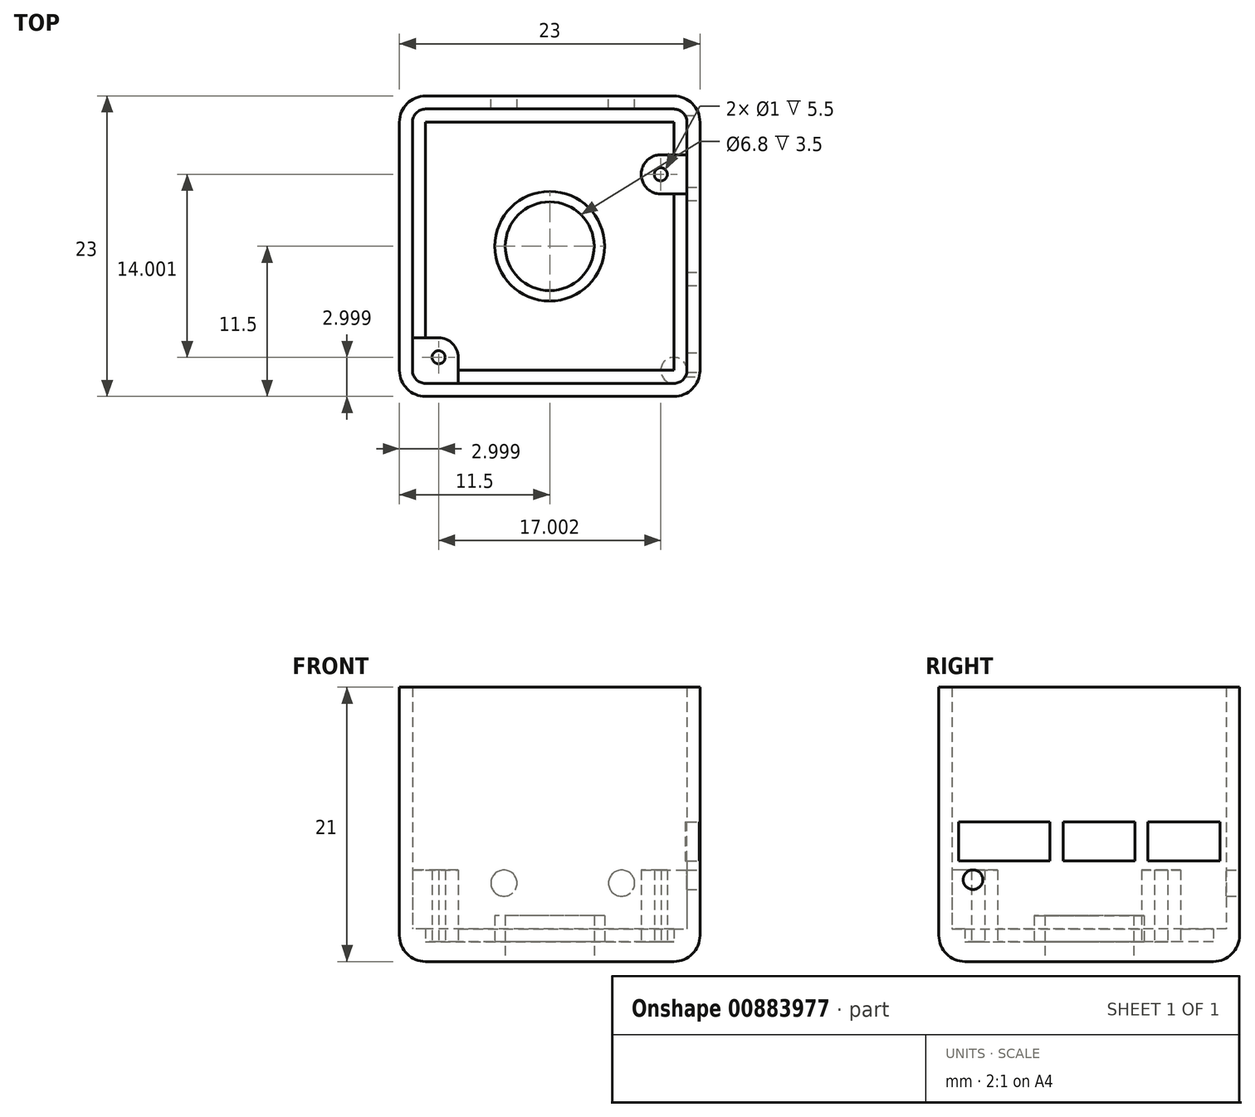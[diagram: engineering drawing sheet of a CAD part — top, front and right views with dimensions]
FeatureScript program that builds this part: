
annotation { "Feature Type Name" : "Feature", "Feature Type Description" : "" }
export const myFeature = defineFeature(function(context is Context, id is Id, definition is map)
    precondition{}
    {
        {
            var Q0;
            Q0=qCreatedBy(makeId("Top.planeOp"),FACE);
            var sketch = newSketch(context, id + "F0", { "sketchPlane" : qUnion([Q0])});
            skLineSegment(sketch, "E0.bottom", {"start": v(9.5, -11.5) * mm, "end": v(-9.5, -11.5) * mm});
            skLineSegment(sketch, "E0.top", {"start": v(9.5, 11.5) * mm, "end": v(-9.5, 11.5) * mm});
            skLineSegment(sketch, "E0.left", {"start": v(11.5, -9.5) * mm, "end": v(11.5, 9.5) * mm});
            skLineSegment(sketch, "E0.right", {"start": v(-11.5, -9.5) * mm, "end": v(-11.5, 9.5) * mm});
            skPoint(sketch, "E0.middle", {"position": v(0, 0) * mm});
            skCircle(sketch, "E1", {"center": v(0, 0) * mm, "radius": 3.4 * mm});
            skLineSegment(sketch, "E2.bottom", {"start": v(8.5, -8.5) * mm, "end": v(-8.5, -8.5) * mm});
            skLineSegment(sketch, "E2.top", {"start": v(8.5, 8.5) * mm, "end": v(-8.5, 8.5) * mm});
            skLineSegment(sketch, "E2.left", {"start": v(8.5, -8.5) * mm, "end": v(8.5, 8.5) * mm});
            skLineSegment(sketch, "E2.right", {"start": v(-8.5, -8.5) * mm, "end": v(-8.5, 8.5) * mm});
            skLineSegment(sketch, "E3", {"start": v(8.5, -8.5) * mm, "end": v(8.5, 5.5) * mm});
            skPoint(sketch, "E4.visualSharp", {"position": v(-11.5, -11.5) * mm});
            skArc(sketch, "E4.filletArc", {"start": v(-11.5, -9.5) * mm, "mid": v(-10.91, -10.91) * mm, "end": v(-9.5, -11.5) * mm});
            skPoint(sketch, "E5.visualSharp", {"position": v(11.5, -11.5) * mm});
            skArc(sketch, "E5.filletArc", {"start": v(9.5, -11.5) * mm, "mid": v(10.91, -10.91) * mm, "end": v(11.5, -9.5) * mm});
            skPoint(sketch, "E6.visualSharp", {"position": v(-11.5, 11.5) * mm});
            skArc(sketch, "E6.filletArc", {"start": v(-9.5, 11.5) * mm, "mid": v(-10.91, 10.91) * mm, "end": v(-11.5, 9.5) * mm});
            skPoint(sketch, "E7.visualSharp", {"position": v(11.5, 11.5) * mm});
            skArc(sketch, "E7.filletArc", {"start": v(11.5, 9.5) * mm, "mid": v(10.91, 10.91) * mm, "end": v(9.5, 11.5) * mm});
            skSolve(sketch);
        }
        {
            var Q0;
            Q0 = qSketchRegion(id + "F0", true);
            var Q1;
            Q1=makeQuery(id+"F0.imprint","IMPRINT",FACE,{"disambiguationData":[TD([[makeQuery(id+"F0.imprint","IMPRINT",EDGE,{"derivedFrom":sQuery(id+"F0.wireOp",EDGE,"E1")}),-1.0]])]});
            extrude(context, id + "F1", {"entities" : qUnion([Q0, Q1]), "depth" : 1.5 * mm, "offsetDistance" : 25 * mm});
        }
        {
            var Q0;
            Q0=makeQuery(id+"F1.opExtrude","CAP_FACE",FACE,{"disambiguationData":[OSD([sQuery(id+"F0.wireOp",EDGE,"E0.bottom"),sQuery(id+"F0.wireOp",EDGE,"E0.top"),sQuery(id+"F0.wireOp",EDGE,"E0.left"),sQuery(id+"F0.wireOp",EDGE,"E0.right"),sQuery(id+"F0.wireOp",EDGE,"E1")])],"isStart":false});
            var sketch = newSketch(context, id + "F2", { "sketchPlane" : qUnion([Q0])});
            skCircle(sketch, "E8", {"center": v(0, 0) * mm, "radius": 4.2 * mm});
            skCircle(sketch, "E9", {"center": v(-8.5, -8.5) * mm, "radius": 0.5 * mm});
            skArc(sketch, "E10", {"start": v(-7, -8.5) * mm, "mid": v(-7.44, -7.44) * mm, "end": v(-8.52, -7) * mm});
            skCircle(sketch, "E11", {"center": v(8.5, 5.5) * mm, "radius": 0.5 * mm});
            skArc(sketch, "E12", {"start": v(8.51, 7) * mm, "mid": v(7, 5.5) * mm, "end": v(8.52, 4) * mm});
            skPoint(sketch, "E13.top.end.orphan", {"position": v(-8.5, 8.5) * mm});
            skPoint(sketch, "E14.trimOffspring.end.orphan", {"position": v(8.5, 8.5) * mm});
            skPoint(sketch, "E15.orphan", {"position": v(8.5, -8.5) * mm});
            skLineSegment(sketch, "E16.0", {"start": v(10.5, -9.5) * mm, "end": v(10.5, 9.5) * mm});
            skArc(sketch, "E16.1", {"start": v(9.5, -10.5) * mm, "mid": v(10.2, -10.2) * mm, "end": v(10.5, -9.5) * mm});
            skArc(sketch, "E16.2", {"start": v(10.5, 9.5) * mm, "mid": v(10.2, 10.2) * mm, "end": v(9.5, 10.5) * mm});
            skLineSegment(sketch, "E16.3", {"start": v(-9.5, -10.5) * mm, "end": v(9.5, -10.5) * mm});
            skLineSegment(sketch, "E16.4", {"start": v(9.5, 10.5) * mm, "end": v(-9.5, 10.5) * mm});
            skArc(sketch, "E16.5", {"start": v(-9.5, 10.5) * mm, "mid": v(-10.2, 10.2) * mm, "end": v(-10.5, 9.5) * mm});
            skLineSegment(sketch, "E16.6", {"start": v(-10.5, 9.5) * mm, "end": v(-10.5, -9.5) * mm});
            skArc(sketch, "E16.7", {"start": v(-10.5, -9.5) * mm, "mid": v(-10.2, -10.2) * mm, "end": v(-9.5, -10.5) * mm});
            skLineSegment(sketch, "E17", {"start": v(8.51, 7) * mm, "end": v(10.5, 7) * mm});
            skLineSegment(sketch, "E18", {"start": v(8.52, 4) * mm, "end": v(10.5, 4) * mm});
            skLineSegment(sketch, "E19", {"start": v(-7, -8.5) * mm, "end": v(-7, -10.5) * mm});
            skLineSegment(sketch, "E20", {"start": v(-8.48, -7) * mm, "end": v(-10.5, -7) * mm});
            skLineSegment(sketch, "E21", {"start": v(-9.5, 9.5) * mm, "end": v(-9.5, -7) * mm});
            skLineSegment(sketch, "E22", {"start": v(-9.5, 9.5) * mm, "end": v(9.5, 9.5) * mm});
            skLineSegment(sketch, "E23", {"start": v(9.5, 9.5) * mm, "end": v(9.5, 7) * mm});
            skPoint(sketch, "E23.endSnap0", {"position": v(9.5, 7) * mm});
            skLineSegment(sketch, "E24", {"start": v(9.5, -9.5) * mm, "end": v(9.5, 4) * mm});
            skLineSegment(sketch, "E25", {"start": v(9.5, -9.5) * mm, "end": v(-7, -9.5) * mm});
            skSolve(sketch);
        }
        {
            var Q0;
            Q0=makeQuery(id+"F2.imprint","IMPRINT",FACE,{"disambiguationData":[TD([[makeQuery(id+"F2.imprint","IMPRINT",EDGE,{"derivedFrom":sQuery(id+"F2.wireOp",EDGE,"E8")}),1.0]])]});
            extrude(context, id + "F3", {"entities" : qUnion([Q0]), "operationType" : NewBodyOperationType.ADD, "depth" : 2 * mm, "offsetDistance" : 25 * mm});
        }
        {
            var Q0;
            Q0=makeQuery(id+"F2.imprint","IMPRINT",FACE,{"disambiguationData":[TD([[makeQuery(id+"F2.imprint","IMPRINT",EDGE,{"derivedFrom":sQuery(id+"F2.wireOp",EDGE,"E9")}),-1.0]])]});
            var Q1;
            Q1=makeQuery(id+"F2.imprint","IMPRINT",FACE,{"disambiguationData":[TD([[makeQuery(id+"F2.imprint","IMPRINT",EDGE,{"derivedFrom":sQuery(id+"F2.wireOp",EDGE,"E11")}),-1.0]])]});
            extrude(context, id + "F4", {"entities" : qUnion([Q0, Q1]), "operationType" : NewBodyOperationType.ADD, "depth" : 5.5 * mm, "offsetDistance" : 25 * mm});
        }
        {
            var Q0;
            {var subQ0=sQuery(id+"F0.wireOp",EDGE,"E0.left");var subQ1=sQuery(id+"F0.wireOp",EDGE,"E7.filletArc");var subQ2=sQuery(id+"F0.wireOp",EDGE,"E6.filletArc");var subQ3=sQuery(id+"F0.wireOp",EDGE,"E5.filletArc");var subQ4=sQuery(id+"F0.wireOp",EDGE,"E4.filletArc");var subQ5=sQuery(id+"F0.wireOp",EDGE,"E0.bottom");var subQ6=sQuery(id+"F0.wireOp",EDGE,"E0.right");var subQ7=sQuery(id+"F0.wireOp",EDGE,"E0.top");Q0=makeQuery(id+"F4.boolean.opBoolean","SPLIT",FACE,{"disambiguationData":[TD([makeQuery(id+"F1.opExtrude","SWEPT_FACE",FACE,{"disambiguationData":[OSD([subQ5])]})])],"derivedFrom":makeQuery(id+"F1.opExtrude","CAP_FACE",FACE,{"disambiguationData":[OSD([subQ5,subQ7,subQ0,subQ6,sQuery(id+"F0.wireOp",EDGE,"E1"),subQ4,subQ3,subQ2,subQ1])],"isStart":false})});}
            var sketch = newSketch(context, id + "F5", { "sketchPlane" : qUnion([Q0])});
            skArc(sketch, "E26.0", {"start": v(10.5, 9.5) * mm, "mid": v(10.2, 10.2) * mm, "end": v(9.5, 10.5) * mm});
            skLineSegment(sketch, "E26.1", {"start": v(10.5, -9.5) * mm, "end": v(10.5, 9.5) * mm});
            skLineSegment(sketch, "E26.2", {"start": v(9.5, 10.5) * mm, "end": v(-9.5, 10.5) * mm});
            skArc(sketch, "E26.3", {"start": v(9.5, -10.5) * mm, "mid": v(10.2, -10.2) * mm, "end": v(10.5, -9.5) * mm});
            skArc(sketch, "E26.4", {"start": v(-9.5, 10.5) * mm, "mid": v(-10.2, 10.2) * mm, "end": v(-10.5, 9.5) * mm});
            skLineSegment(sketch, "E26.5", {"start": v(-10.5, -9.5) * mm, "end": v(-10.5, 9.5) * mm});
            skArc(sketch, "E26.6", {"start": v(-10.5, -9.5) * mm, "mid": v(-10.2, -10.2) * mm, "end": v(-9.5, -10.5) * mm});
            skLineSegment(sketch, "E26.7", {"start": v(9.5, -10.5) * mm, "end": v(-9.5, -10.5) * mm});
            skSolve(sketch);
        }
        {
            var Q0;
            Q0=makeQuery(id+"F5.imprint","IMPRINT",FACE,{"disambiguationData":[TD([[makeQuery(id+"F5.imprint","IMPRINT",EDGE,{"derivedFrom":sQuery(id+"F5.wireOp",EDGE,"E26.0")}),-1.0]])]});
            extrude(context, id + "F6", {"entities" : qUnion([Q0]), "operationType" : NewBodyOperationType.ADD, "depth" : 19.5 * mm, "offsetDistance" : 25 * mm});
        }
        {
            var Q0;
            {var subQ0=sQuery(id+"F0.wireOp",EDGE,"E0.top");Q0=makeQuery(id+"F6.boolean.opBoolean","MERGE",FACE,{"derivedFrom":[makeQuery(id+"F1.opExtrude","SWEPT_FACE",FACE,{"disambiguationData":[OSD([subQ0])]}),makeQuery(id+"F6.opExtrude","SWEPT_FACE",FACE,{"disambiguationData":[OSD([subQ0])]})]});}
            var sketch = newSketch(context, id + "F7", { "sketchPlane" : qUnion([Q0])});
            skLineSegment(sketch, "E27", {"start": v(0, 0) * mm, "end": v(0, 6) * mm});
            skLineSegment(sketch, "E28", {"start": v(0, 6) * mm, "end": v(-5.5, 6) * mm});
            skLineSegment(sketch, "E29", {"start": v(0, 6) * mm, "end": v(3.5, 6) * mm});
            skCircle(sketch, "E30", {"center": v(-5.5, 6) * mm, "radius": 1 * mm});
            skCircle(sketch, "E31", {"center": v(3.5, 6) * mm, "radius": 1 * mm});
            skSolve(sketch);
        }
        {
            var Q0;
            {var subQ0=sQuery(id+"F0.wireOp",EDGE,"E0.left");Q0=makeQuery(id+"F6.boolean.opBoolean","MERGE",FACE,{"derivedFrom":[makeQuery(id+"F1.opExtrude","SWEPT_FACE",FACE,{"disambiguationData":[OSD([subQ0])]}),makeQuery(id+"F6.opExtrude","SWEPT_FACE",FACE,{"disambiguationData":[OSD([subQ0])]})]});}
            var sketch = newSketch(context, id + "F8", { "sketchPlane" : qUnion([Q0])});
            skLineSegment(sketch, "E32", {"start": v(0, 7.7) * mm, "end": v(10, 7.7) * mm});
            skLineSegment(sketch, "E33", {"start": v(10, 7.7) * mm, "end": v(10, 10.7) * mm});
            skLineSegment(sketch, "E34", {"start": v(10, 10.7) * mm, "end": v(-10, 10.7) * mm});
            skLineSegment(sketch, "E35", {"start": v(-10, 10.7) * mm, "end": v(-10, 7.7) * mm});
            skLineSegment(sketch, "E36", {"start": v(-10, 7.7) * mm, "end": v(0, 7.7) * mm});
            skCircle(sketch, "E37", {"center": v(-8.9, 6.27) * mm, "radius": 0.75 * mm});
            skLineSegment(sketch, "E38", {"start": v(10, 7.7) * mm, "end": v(-2, 7.7) * mm});
            skLineSegment(sketch, "E39", {"start": v(-2, 7.7) * mm, "end": v(-2, 10.7) * mm});
            skLineSegment(sketch, "E40", {"start": v(-2, 10.7) * mm, "end": v(-3, 10.7) * mm});
            skLineSegment(sketch, "E41", {"start": v(-3, 10.7) * mm, "end": v(-3, 7.7) * mm});
            skLineSegment(sketch, "E42", {"start": v(10, 7.7) * mm, "end": v(4.5, 7.7) * mm});
            skLineSegment(sketch, "E43", {"start": v(4.5, 7.7) * mm, "end": v(4.5, 10.7) * mm});
            skLineSegment(sketch, "E44", {"start": v(4.5, 10.7) * mm, "end": v(3.5, 10.7) * mm});
            skLineSegment(sketch, "E45", {"start": v(3.5, 10.7) * mm, "end": v(3.5, 7.7) * mm});
            skSolve(sketch);
        }
        {
            var Q0;
            {var subQ0=sQuery(id+"F8.wireOp",EDGE,"E39");Q0=makeQuery(id+"F8.imprint","IMPRINT",FACE,{"disambiguationData":[TD([[makeQuery(id+"F8.imprint","IMPRINT",EDGE,{"derivedFrom":subQ0}),-1.0]])]});}
            var Q1;
            {var subQ0=sQuery(id+"F8.wireOp",EDGE,"E33");Q1=makeQuery(id+"F8.imprint","IMPRINT",FACE,{"disambiguationData":[TD([[makeQuery(id+"F8.imprint","IMPRINT",EDGE,{"derivedFrom":subQ0}),1.0]])]});}
            var Q2;
            {var subQ0=sQuery(id+"F8.wireOp",EDGE,"E35");Q2=makeQuery(id+"F8.imprint","IMPRINT",FACE,{"disambiguationData":[TD([[makeQuery(id+"F8.imprint","IMPRINT",EDGE,{"derivedFrom":subQ0}),1.0]])]});}
            var Q3;
            {var subQ0=sQuery(id+"F8.wireOp",EDGE,"E37");var subQ1=sQuery(id+"F0.wireOp",EDGE,"E5.filletArc");var subQ2=sQuery(id+"F0.wireOp",EDGE,"E0.left");var subQ3=makeQuery(id+"F6.boolean.opBoolean","MERGE",EDGE,{"derivedFrom":[makeQuery(id+"F1.opExtrude","SWEPT_EDGE",EDGE,{"disambiguationData":[OSD([subQ2,subQ1])]}),makeQuery(id+"F6.opExtrude","SWEPT_EDGE",EDGE,{"disambiguationData":[OSD([subQ2,subQ1])]})]});var subQ4=makeQuery(id+"F8.imprint","INTERSECT",VERTEX,{"disambiguationData":[OD(0.0)],"derivedFrom":[subQ3,subQ0]});Q3=makeQuery(id+"F8.imprint","IMPRINT",FACE,{"disambiguationData":[TD([[makeQuery(id+"F8.imprint","IMPRINT",EDGE,{"disambiguationData":[TD([[subQ4,1.0]])],"derivedFrom":subQ0}),1.0]])]});}
            var Q4;
            {var subQ0=sQuery(id+"F8.wireOp",EDGE,"E37");var subQ1=sQuery(id+"F0.wireOp",EDGE,"E5.filletArc");var subQ2=sQuery(id+"F0.wireOp",EDGE,"E0.left");var subQ3=makeQuery(id+"F6.boolean.opBoolean","MERGE",EDGE,{"derivedFrom":[makeQuery(id+"F1.opExtrude","SWEPT_EDGE",EDGE,{"disambiguationData":[OSD([subQ2,subQ1])]}),makeQuery(id+"F6.opExtrude","SWEPT_EDGE",EDGE,{"disambiguationData":[OSD([subQ2,subQ1])]})]});var subQ4=makeQuery(id+"F8.imprint","INTERSECT",VERTEX,{"disambiguationData":[OD(0.0)],"derivedFrom":[subQ3,subQ0]});Q4=makeQuery(id+"F8.imprint","IMPRINT",FACE,{"disambiguationData":[TD([[makeQuery(id+"F8.imprint","IMPRINT",EDGE,{"disambiguationData":[TD([[subQ4,-1.0]])],"derivedFrom":subQ0}),1.0]])]});}
            var Q5;
            {var subQ0=sQuery(id+"F8.wireOp",EDGE,"E43");Q5=makeQuery(id+"F8.imprint","IMPRINT",FACE,{"disambiguationData":[TD([[makeQuery(id+"F8.imprint","IMPRINT",EDGE,{"derivedFrom":subQ0}),-1.0]])]});}
            var Q6;
            {var subQ0=sQuery(id+"F8.wireOp",EDGE,"E41");Q6=makeQuery(id+"F8.imprint","IMPRINT",FACE,{"disambiguationData":[TD([[makeQuery(id+"F8.imprint","IMPRINT",EDGE,{"derivedFrom":subQ0}),-1.0]])]});}
            extrude(context, id + "F9", {"entities" : qUnion([Q0, Q1, Q2, Q3, Q4, Q5, Q6]), "operationType" : NewBodyOperationType.REMOVE, "oppositeDirection" : true, "depth" : 5 * mm, "offsetDistance" : 25 * mm});
        }
        {
            var Q0;
            Q0=makeQuery(id+"F7.imprint","IMPRINT",FACE,{"disambiguationData":[TD([[makeQuery(id+"F7.imprint","IMPRINT",EDGE,{"derivedFrom":sQuery(id+"F7.wireOp",EDGE,"E30")}),1.0]])]});
            var Q1;
            Q1=makeQuery(id+"F7.imprint","IMPRINT",FACE,{"disambiguationData":[TD([[makeQuery(id+"F7.imprint","IMPRINT",EDGE,{"derivedFrom":sQuery(id+"F7.wireOp",EDGE,"E31")}),1.0]])]});
            extrude(context, id + "F10", {"entities" : qUnion([Q0, Q1]), "operationType" : NewBodyOperationType.REMOVE, "oppositeDirection" : true, "depth" : 5 * mm, "offsetDistance" : 25 * mm});
        }
        {
            var Q0;
            Q0=makeQuery(id+"F1.opExtrude","CAP_EDGE",EDGE,{"disambiguationData":[OSD([sQuery(id+"F0.wireOp",EDGE,"E0.bottom")])],"isStart":true});
            fillet(context, id + "F11", {"entities" : qUnion([Q0]), "radius" : 2 * mm, "tangentPropagation" : true, "allowEdgeOverflow" : false});
        }
        {
            var Q0;
            Q0 = qSketchRegion(id + "F2", true);
            extrude(context, id + "F12", {"entities" : qUnion([Q0]), "operationType" : NewBodyOperationType.ADD, "depth" : 1 * mm, "offsetDistance" : 25 * mm});
        }
    });
